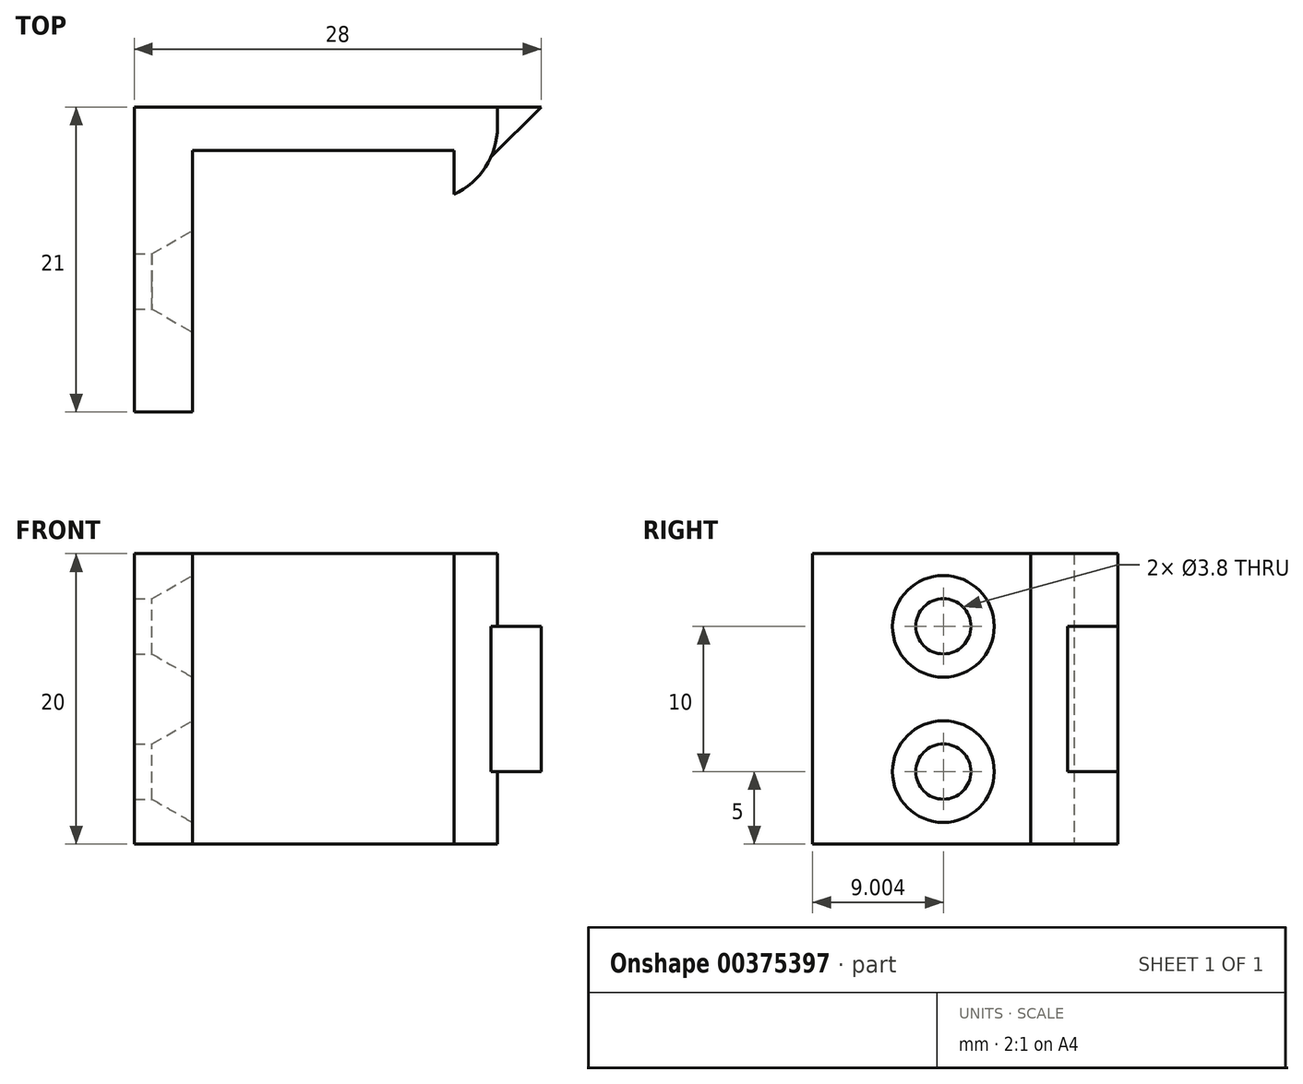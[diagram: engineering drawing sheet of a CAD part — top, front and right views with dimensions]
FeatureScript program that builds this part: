
annotation { "Feature Type Name" : "Feature", "Feature Type Description" : "" }
export const myFeature = defineFeature(function(context is Context, id is Id, definition is map)
    precondition{}
    {
        {
            var Q0;
            Q0=qCreatedBy(makeId("Top.planeOp"),FACE);
            var sketch = newSketch(context, id + "F0", { "sketchPlane" : qUnion([Q0])});
            skLineSegment(sketch, "E0", {"start": v(-23.2, -16.99) * mm, "end": v(-19.2, -16.99) * mm});
            skLineSegment(sketch, "E1", {"start": v(-19.2, -16.99) * mm, "end": v(-19.2, 1.01) * mm});
            skLineSegment(sketch, "E2", {"start": v(-19.2, 1.01) * mm, "end": v(-1.2, 1.01) * mm});
            skLineSegment(sketch, "E3", {"start": v(-1.2, 1.01) * mm, "end": v(-1.2, -1.99) * mm});
            skLineSegment(sketch, "E4", {"start": v(-1.2, -1.99) * mm, "end": v(1.8, -1.99) * mm});
            skLineSegment(sketch, "E5", {"start": v(1.8, -1.99) * mm, "end": v(1.8, 4.01) * mm});
            skLineSegment(sketch, "E6", {"start": v(1.8, 4.01) * mm, "end": v(-23.2, 4.01) * mm});
            skLineSegment(sketch, "E7", {"start": v(-23.2, 4.01) * mm, "end": v(-23.2, -16.99) * mm});
            skLineSegment(sketch, "E8", {"start": v(1.8, 4.01) * mm, "end": v(4.8, 4.01) * mm});
            skLineSegment(sketch, "E9", {"start": v(4.8, 4.01) * mm, "end": v(1.8, 1.01) * mm});
            skSolve(sketch);
        }
        {
            var Q0;
            Q0=makeQuery(id+"F0.imprint","IMPRINT",FACE,{"disambiguationData":[TD([[makeQuery(id+"F0.imprint","IMPRINT",EDGE,{"derivedFrom":sQuery(id+"F0.wireOp",EDGE,"E0")}),1.0]])]});
            extrude(context, id + "F1", {"entities" : qUnion([Q0]), "depth" : 20 * mm});
        }
        {
            var Q0;
            {var subQ0=sQuery(id+"F0.wireOp",EDGE,"E8");Q0=makeQuery(id+"F0.imprint","IMPRINT",FACE,{"disambiguationData":[TD([[makeQuery(id+"F0.imprint","IMPRINT",EDGE,{"derivedFrom":subQ0}),-1.0]])]});}
            extrude(context, id + "F2", {"entities" : qUnion([Q0]), "operationType" : NewBodyOperationType.ADD, "depth" : 15 * mm});
        }
        {
            var Q0;
            {var subQ0=sQuery(id+"F0.wireOp",EDGE,"E8");Q0=makeQuery(id+"F0.imprint","IMPRINT",FACE,{"disambiguationData":[TD([[makeQuery(id+"F0.imprint","IMPRINT",EDGE,{"derivedFrom":subQ0}),-1.0]])]});}
            extrude(context, id + "F3", {"entities" : qUnion([Q0]), "operationType" : NewBodyOperationType.REMOVE, "depth" : 5 * mm});
        }
        {
            var Q0;
            Q0=makeQuery(id+"F1.opExtrude","SWEPT_FACE",FACE,{"disambiguationData":[OSD([sQuery(id+"F0.wireOp",EDGE,"E1")])]});
            var sketch = newSketch(context, id + "F4", { "sketchPlane" : qUnion([Q0])});
            skLineSegment(sketch, "E10", {"start": v(-16.99, 20) * mm, "end": v(-7.99, 20) * mm});
            skLineSegment(sketch, "E11", {"start": v(-7.99, 20) * mm, "end": v(-7.99, 15) * mm});
            skPoint(sketch, "E11.endSnap0", {"position": v(-7.99, 0) * mm});
            skLineSegment(sketch, "E12", {"start": v(-7.99, 15) * mm, "end": v(-7.99, 5) * mm});
            skSolve(sketch);
        }
        {
            var Q0;
            Q0=sQuery(id+"F4.wireOp",VERTEX,"E12.start");
            var Q1;
            Q1=sQuery(id+"F4.wireOp",VERTEX,"E12.end");
            var Q2;
            Q2=makeQuery(id+"F1.opExtrude","SWEPT_BODY",BODY,{"disambiguationData":[OSD([sQuery(id+"F0.wireOp",EDGE,"E0"),sQuery(id+"F0.wireOp",EDGE,"E1"),sQuery(id+"F0.wireOp",EDGE,"E2"),sQuery(id+"F0.wireOp",EDGE,"E3"),sQuery(id+"F0.wireOp",EDGE,"E4"),sQuery(id+"F0.wireOp",EDGE,"E5"),sQuery(id+"F0.wireOp",EDGE,"E6"),sQuery(id+"F0.wireOp",EDGE,"E7")])]});
            hole(context, id + "F5", {"style" : HoleStyle.C_SINK, "endStyle" : HoleEndStyle.BLIND, "holeDiameter" : 3.8 * mm, "cSinkDiameter" : 7 * mm, "cSinkAngle" : 60 * degree, "holeDepth" : 20 * mm, "isTappedThrough" : true, "tappedDepth" : 12.7 * mm, "tapClearance" : 3, "locations" : qUnion([Q0, Q1]), "scope" : qUnion([Q2])});
        }
        {
            var Q0;
            Q0=makeQuery(id+"F1.opExtrude","SWEPT_EDGE",EDGE,{"disambiguationData":[OSD([sQuery(id+"F0.wireOp",EDGE,"E4"),sQuery(id+"F0.wireOp",EDGE,"E5")])]});
            fillet(context, id + "F6", {"entities" : qUnion([Q0]), "radius" : 5.08 * mm, "tangentPropagation" : true, "allowEdgeOverflow" : false});
        }
    });
